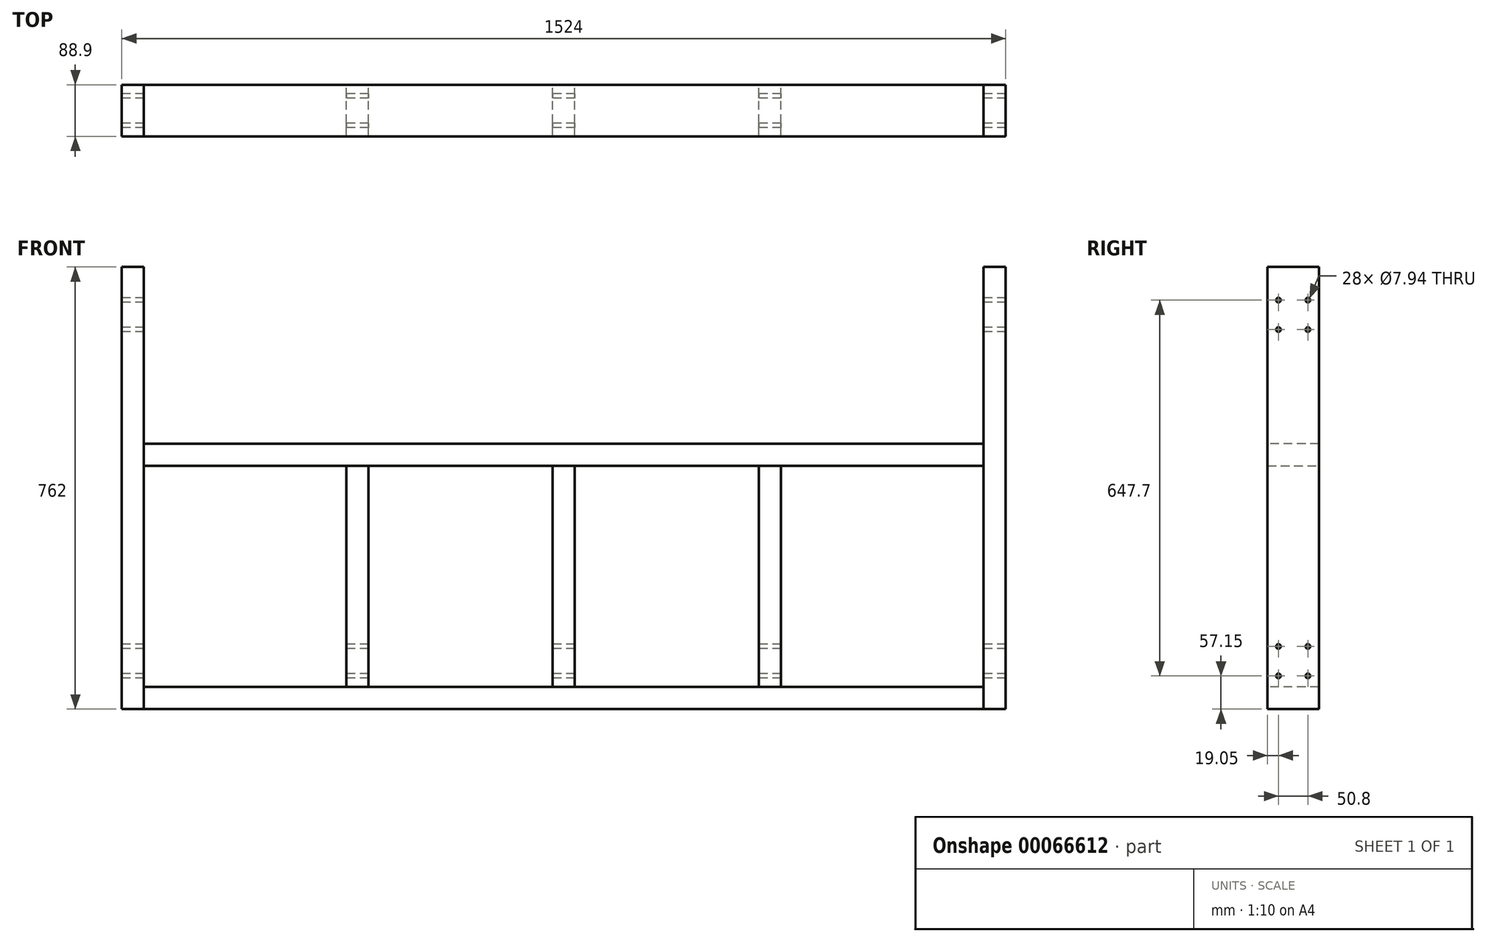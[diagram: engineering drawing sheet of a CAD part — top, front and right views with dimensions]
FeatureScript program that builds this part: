
annotation { "Feature Type Name" : "Feature", "Feature Type Description" : "" }
export const myFeature = defineFeature(function(context is Context, id is Id, definition is map)
    precondition{}
    {
        {
            var Q0;
            Q0=qCreatedBy(makeId("Top.planeOp"),FACE);
            var sketch = newSketch(context, id + "F0", { "sketchPlane" : qUnion([Q0])});
            skLineSegment(sketch, "E0.rect.bottom", {"start": v(-723.9, 44.45) * mm, "end": v(-762, 44.45) * mm});
            skLineSegment(sketch, "E0.rect.top", {"start": v(-723.9, -44.45) * mm, "end": v(-762, -44.45) * mm});
            skLineSegment(sketch, "E0.rect.left", {"start": v(-723.9, 44.45) * mm, "end": v(-723.9, -44.45) * mm});
            skLineSegment(sketch, "E0.rect.right", {"start": v(-762, 44.45) * mm, "end": v(-762, -44.45) * mm});
            skPoint(sketch, "E0.rect.middle", {"position": v(-742.95, 0) * mm});
            skLineSegment(sketch, "E1.rect.bottom", {"start": v(723.9, 44.45) * mm, "end": v(762, 44.45) * mm});
            skLineSegment(sketch, "E1.rect.top", {"start": v(723.9, -44.45) * mm, "end": v(762, -44.45) * mm});
            skLineSegment(sketch, "E1.rect.left", {"start": v(723.9, 44.45) * mm, "end": v(723.9, -44.45) * mm});
            skLineSegment(sketch, "E1.rect.right", {"start": v(762, 44.45) * mm, "end": v(762, -44.45) * mm});
            skPoint(sketch, "E1.rect.middle", {"position": v(742.95, 0) * mm});
            skLineSegment(sketch, "E2", {"start": v(-723.9, 0) * mm, "end": v(723.9, 0) * mm});
            skPoint(sketch, "E3.0", {"position": v(0, 0) * mm});
            skSolve(sketch);
        }
        {
            var Q0;
            Q0 = qSketchRegion(id + "F0", true);
            extrude(context, id + "F1", {"entities" : qUnion([Q0]), "depth" : 762 * mm});
        }
        {
            var Q0;
            Q0=makeQuery(id+"F1.opExtrude","SWEPT_FACE",FACE,{"disambiguationData":[OSD([sQuery(id+"F0.wireOp",EDGE,"E0.rect.left")])]});
            var sketch = newSketch(context, id + "F2", { "sketchPlane" : qUnion([Q0])});
            skLineSegment(sketch, "E4.bottom", {"start": v(44.45, 0) * mm, "end": v(-44.45, 0) * mm});
            skLineSegment(sketch, "E4.top", {"start": v(44.45, 38.1) * mm, "end": v(-44.45, 38.1) * mm});
            skLineSegment(sketch, "E4.left", {"start": v(44.45, 0) * mm, "end": v(44.45, 38.1) * mm});
            skLineSegment(sketch, "E4.right", {"start": v(-44.45, 0) * mm, "end": v(-44.45, 38.1) * mm});
            skLineSegment(sketch, "E5.bottom", {"start": v(44.45, 419.1) * mm, "end": v(-44.45, 419.1) * mm});
            skLineSegment(sketch, "E5.top", {"start": v(44.45, 457.2) * mm, "end": v(-44.45, 457.2) * mm});
            skLineSegment(sketch, "E5.left", {"start": v(44.45, 419.1) * mm, "end": v(44.45, 457.2) * mm});
            skLineSegment(sketch, "E5.right", {"start": v(-44.45, 419.1) * mm, "end": v(-44.45, 457.2) * mm});
            skSolve(sketch);
        }
        {
            var Q0;
            Q0 = qSketchRegion(id + "F2", true);
            extrude(context, id + "F3", {"entities" : qUnion([Q0]), "endBound" : BoundingType.UP_TO_NEXT, "depth" : 25.4 * mm});
        }
        {
            var Q0;
            Q0=makeQuery(id+"F3.opExtrude","SWEPT_FACE",FACE,{"disambiguationData":[OSD([sQuery(id+"F2.wireOp",EDGE,"E4.top")])]});
            var sketch = newSketch(context, id + "F4", { "sketchPlane" : qUnion([Q0])});
            skLineSegment(sketch, "E6.rect.bottom", {"start": v(19.05, 44.45) * mm, "end": v(-19.05, 44.45) * mm});
            skLineSegment(sketch, "E6.rect.top", {"start": v(19.05, -44.45) * mm, "end": v(-19.05, -44.45) * mm});
            skLineSegment(sketch, "E6.rect.left", {"start": v(19.05, 44.45) * mm, "end": v(19.05, -44.45) * mm});
            skLineSegment(sketch, "E6.rect.right", {"start": v(-19.05, 44.45) * mm, "end": v(-19.05, -44.45) * mm});
            skPoint(sketch, "E6.rect.middle", {"position": v(0, 0) * mm});
            skLineSegment(sketch, "E7.rect.bottom", {"start": v(-336.55, 44.45) * mm, "end": v(-374.65, 44.45) * mm});
            skLineSegment(sketch, "E7.rect.top", {"start": v(-336.55, -44.45) * mm, "end": v(-374.65, -44.45) * mm});
            skLineSegment(sketch, "E7.rect.left", {"start": v(-336.55, 44.45) * mm, "end": v(-336.55, -44.45) * mm});
            skLineSegment(sketch, "E7.rect.right", {"start": v(-374.65, 44.45) * mm, "end": v(-374.65, -44.45) * mm});
            skPoint(sketch, "E7.rect.middle", {"position": v(-355.6, 0) * mm});
            skLineSegment(sketch, "E8.rect.bottom", {"start": v(336.55, 44.45) * mm, "end": v(374.65, 44.45) * mm});
            skLineSegment(sketch, "E8.rect.top", {"start": v(336.55, -44.45) * mm, "end": v(374.65, -44.45) * mm});
            skLineSegment(sketch, "E8.rect.left", {"start": v(336.55, 44.45) * mm, "end": v(336.55, -44.45) * mm});
            skLineSegment(sketch, "E8.rect.right", {"start": v(374.65, 44.45) * mm, "end": v(374.65, -44.45) * mm});
            skPoint(sketch, "E8.rect.middle", {"position": v(355.6, 0) * mm});
            skSolve(sketch);
        }
        {
            var Q0;
            Q0 = qSketchRegion(id + "F4", true);
            extrude(context, id + "F5", {"entities" : qUnion([Q0]), "endBound" : BoundingType.UP_TO_NEXT, "depth" : 25.4 * mm});
        }
        {
            var Q0;
            Q0=makeQuery(id+"F1.opExtrude","SWEPT_FACE",FACE,{"disambiguationData":[OSD([sQuery(id+"F0.wireOp",EDGE,"E0.rect.right")])]});
            var sketch = newSketch(context, id + "F6", { "sketchPlane" : qUnion([Q0])});
            skLineSegment(sketch, "E9.rect.bottom", {"start": v(44.45, 723.9) * mm, "end": v(-44.45, 723.9) * mm, "construction": true});
            skLineSegment(sketch, "E9.rect.top", {"start": v(44.45, 635) * mm, "end": v(-44.45, 635) * mm, "construction": true});
            skLineSegment(sketch, "E9.rect.left", {"start": v(44.45, 723.9) * mm, "end": v(44.45, 635) * mm, "construction": true});
            skLineSegment(sketch, "E9.rect.right", {"start": v(-44.45, 723.9) * mm, "end": v(-44.45, 635) * mm, "construction": true});
            skPoint(sketch, "E9.rect.middle", {"position": v(0, 679.45) * mm});
            skLineSegment(sketch, "E10.rect.bottom", {"start": v(44.45, 38.1) * mm, "end": v(-44.45, 38.1) * mm, "construction": true});
            skLineSegment(sketch, "E10.rect.top", {"start": v(44.45, 127) * mm, "end": v(-44.45, 127) * mm, "construction": true});
            skLineSegment(sketch, "E10.rect.left", {"start": v(44.45, 38.1) * mm, "end": v(44.45, 127) * mm, "construction": true});
            skLineSegment(sketch, "E10.rect.right", {"start": v(-44.45, 38.1) * mm, "end": v(-44.45, 127) * mm, "construction": true});
            skPoint(sketch, "E10.rect.middle", {"position": v(0, 82.55) * mm});
            skLineSegment(sketch, "E11.rect.bottom", {"start": v(-25.4, 704.85) * mm, "end": v(25.4, 704.85) * mm, "construction": true});
            skLineSegment(sketch, "E11.rect.top", {"start": v(-25.4, 654.05) * mm, "end": v(25.4, 654.05) * mm, "construction": true});
            skLineSegment(sketch, "E11.rect.left", {"start": v(-25.4, 704.85) * mm, "end": v(-25.4, 654.05) * mm, "construction": true});
            skLineSegment(sketch, "E11.rect.right", {"start": v(25.4, 704.85) * mm, "end": v(25.4, 654.05) * mm, "construction": true});
            skLineSegment(sketch, "E12.rect.bottom", {"start": v(-25.4, 107.95) * mm, "end": v(25.4, 107.95) * mm, "construction": true});
            skLineSegment(sketch, "E12.rect.top", {"start": v(-25.4, 57.15) * mm, "end": v(25.4, 57.15) * mm, "construction": true});
            skLineSegment(sketch, "E12.rect.left", {"start": v(-25.4, 107.95) * mm, "end": v(-25.4, 57.15) * mm, "construction": true});
            skLineSegment(sketch, "E12.rect.right", {"start": v(25.4, 107.95) * mm, "end": v(25.4, 57.15) * mm, "construction": true});
            skCircle(sketch, "E13", {"center": v(-25.4, 704.85) * mm, "radius": 3.97 * mm});
            skCircle(sketch, "E14", {"center": v(-25.4, 654.05) * mm, "radius": 3.97 * mm});
            skCircle(sketch, "E15", {"center": v(25.4, 654.05) * mm, "radius": 3.97 * mm});
            skCircle(sketch, "E16", {"center": v(25.4, 704.85) * mm, "radius": 3.97 * mm});
            skCircle(sketch, "E17", {"center": v(-25.4, 107.95) * mm, "radius": 3.97 * mm});
            skCircle(sketch, "E18", {"center": v(25.4, 107.95) * mm, "radius": 3.97 * mm});
            skCircle(sketch, "E19", {"center": v(25.4, 57.15) * mm, "radius": 3.97 * mm});
            skCircle(sketch, "E20", {"center": v(-25.4, 57.15) * mm, "radius": 3.97 * mm});
            skSolve(sketch);
        }
        {
            var Q0;
            Q0=makeQuery(id+"F6.imprint","IMPRINT",FACE,{"disambiguationData":[TD([[makeQuery(id+"F6.imprint","IMPRINT",EDGE,{"derivedFrom":sQuery(id+"F6.wireOp",EDGE,"E20")}),1.0]])]});
            var Q1;
            Q1=makeQuery(id+"F6.imprint","IMPRINT",FACE,{"disambiguationData":[TD([[makeQuery(id+"F6.imprint","IMPRINT",EDGE,{"derivedFrom":sQuery(id+"F6.wireOp",EDGE,"E17")}),1.0]])]});
            var Q2;
            Q2=makeQuery(id+"F6.imprint","IMPRINT",FACE,{"disambiguationData":[TD([[makeQuery(id+"F6.imprint","IMPRINT",EDGE,{"derivedFrom":sQuery(id+"F6.wireOp",EDGE,"E18")}),1.0]])]});
            var Q3;
            Q3=makeQuery(id+"F6.imprint","IMPRINT",FACE,{"disambiguationData":[TD([[makeQuery(id+"F6.imprint","IMPRINT",EDGE,{"derivedFrom":sQuery(id+"F6.wireOp",EDGE,"E19")}),1.0]])]});
            var Q4;
            Q4=makeQuery(id+"F6.imprint","IMPRINT",FACE,{"disambiguationData":[TD([[makeQuery(id+"F6.imprint","IMPRINT",EDGE,{"derivedFrom":sQuery(id+"F6.wireOp",EDGE,"E14")}),1.0]])]});
            var Q5;
            Q5=makeQuery(id+"F6.imprint","IMPRINT",FACE,{"disambiguationData":[TD([[makeQuery(id+"F6.imprint","IMPRINT",EDGE,{"derivedFrom":sQuery(id+"F6.wireOp",EDGE,"E13")}),1.0]])]});
            var Q6;
            Q6=makeQuery(id+"F6.imprint","IMPRINT",FACE,{"disambiguationData":[TD([[makeQuery(id+"F6.imprint","IMPRINT",EDGE,{"derivedFrom":sQuery(id+"F6.wireOp",EDGE,"E16")}),1.0]])]});
            var Q7;
            Q7=makeQuery(id+"F6.imprint","IMPRINT",FACE,{"disambiguationData":[TD([[makeQuery(id+"F6.imprint","IMPRINT",EDGE,{"derivedFrom":sQuery(id+"F6.wireOp",EDGE,"E15")}),1.0]])]});
            var Q8;
            Q8=sQuery(id+"F6.wireOp",EDGE,"E20");
            var Q9;
            Q9=sQuery(id+"F6.wireOp",EDGE,"E19");
            var Q10;
            Q10=sQuery(id+"F6.wireOp",EDGE,"E18");
            var Q11;
            Q11=sQuery(id+"F6.wireOp",EDGE,"E17");
            var Q12;
            Q12=sQuery(id+"F6.wireOp",EDGE,"E13");
            var Q13;
            Q13=sQuery(id+"F6.wireOp",EDGE,"E14");
            var Q14;
            Q14=sQuery(id+"F6.wireOp",EDGE,"E15");
            var Q15;
            Q15=sQuery(id+"F6.wireOp",EDGE,"E16");
            extrude(context, id + "F7", {"entities" : qUnion([Q0, Q1, Q2, Q3, Q4, Q5, Q6, Q7]), "operationType" : NewBodyOperationType.REMOVE, "surfaceEntities" : qUnion([Q8, Q9, Q10, Q11, Q12, Q13, Q14, Q15]), "endBound" : BoundingType.THROUGH_ALL, "oppositeDirection" : true, "depth" : 25.4 * mm});
        }
    });
